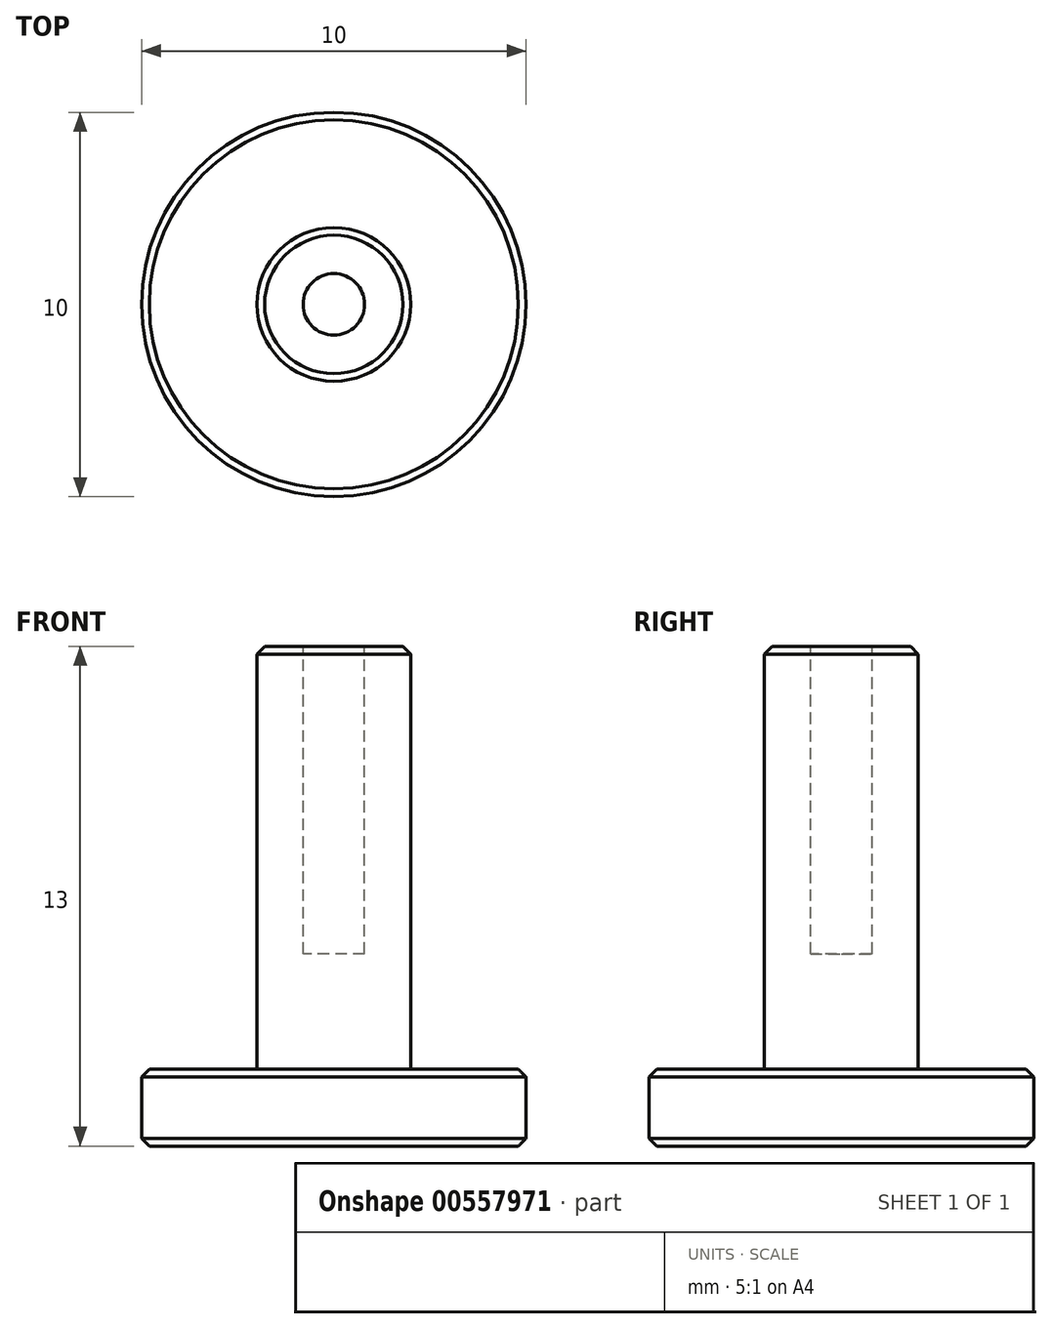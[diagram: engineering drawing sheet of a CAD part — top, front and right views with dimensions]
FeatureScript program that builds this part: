
annotation { "Feature Type Name" : "Feature", "Feature Type Description" : "" }
export const myFeature = defineFeature(function(context is Context, id is Id, definition is map)
    precondition{}
    {
        {
            var Q0;
            Q0=qCreatedBy(makeId("Top.planeOp"),FACE);
            var sketch = newSketch(context, id + "F0", { "sketchPlane" : qUnion([Q0])});
            skCircle(sketch, "E0", {"center": v(0, 0) * mm, "radius": 5 * mm});
            skSolve(sketch);
        }
        {
            var Q0;
            Q0=makeQuery(id+"F0.imprint","IMPRINT",FACE,{"disambiguationData":[TD([[makeQuery(id+"F0.imprint","IMPRINT",EDGE,{"derivedFrom":sQuery(id+"F0.wireOp",EDGE,"E0")}),1.0]])]});
            extrude(context, id + "F1", {"entities" : qUnion([Q0]), "depth" : 2 * mm, "offsetDistance" : 25 * mm});
        }
        {
            var Q0;
            Q0=makeQuery(id+"F1.opExtrude","CAP_FACE",FACE,{"disambiguationData":[OSD([sQuery(id+"F0.wireOp",EDGE,"E0")])],"isStart":false});
            var sketch = newSketch(context, id + "F2", { "sketchPlane" : qUnion([Q0])});
            skCircle(sketch, "E1", {"center": v(0, 0) * mm, "radius": 2 * mm});
            skSolve(sketch);
        }
        {
            var Q0;
            Q0 = qSketchRegion(id + "F2", true);
            extrude(context, id + "F3", {"entities" : qUnion([Q0]), "operationType" : NewBodyOperationType.ADD, "depth" : 11 * mm, "offsetDistance" : 25 * mm});
        }
        {
            var Q0;
            Q0=makeQuery(id+"F3.opExtrude","CAP_FACE",FACE,{"disambiguationData":[OSD([sQuery(id+"F2.wireOp",EDGE,"E1")])],"isStart":false});
            var sketch = newSketch(context, id + "F4", { "sketchPlane" : qUnion([Q0])});
            skCircle(sketch, "E2", {"center": v(0, 0) * mm, "radius": 0.8 * mm});
            skSolve(sketch);
        }
        {
            var Q0;
            Q0=makeQuery(id+"F4.imprint","IMPRINT",FACE,{"disambiguationData":[TD([[makeQuery(id+"F4.imprint","IMPRINT",EDGE,{"derivedFrom":sQuery(id+"F4.wireOp",EDGE,"E2")}),1.0]])]});
            extrude(context, id + "F5", {"entities" : qUnion([Q0]), "operationType" : NewBodyOperationType.REMOVE, "oppositeDirection" : true, "depth" : 8 * mm, "offsetDistance" : 25 * mm});
        }
        {
            var Q0;
            Q0=makeQuery(id+"F3.opExtrude","CAP_EDGE",EDGE,{"disambiguationData":[OSD([sQuery(id+"F2.wireOp",EDGE,"E1")])],"isStart":false});
            var Q1;
            Q1=makeQuery(id+"F1.opExtrude","CAP_EDGE",EDGE,{"disambiguationData":[OSD([sQuery(id+"F0.wireOp",EDGE,"E0")])],"isStart":false});
            var Q2;
            Q2=makeQuery(id+"F5.boolean.opBoolean","COPY",EDGE,{"derivedFrom":makeQuery(id+"F5.opExtrude","CAP_EDGE",EDGE,{"disambiguationData":[OSD([sQuery(id+"F4.wireOp",EDGE,"E2")])],"isStart":true})});
            var Q3;
            Q3=makeQuery(id+"F1.opExtrude","CAP_EDGE",EDGE,{"disambiguationData":[OSD([sQuery(id+"F0.wireOp",EDGE,"E0")])],"isStart":true});
            chamfer(context, id + "F6", {"entities" : qUnion([Q0, Q1, Q2, Q3]), "width" : 0.2 * mm, "tangentPropagation" : true});
        }
    });
